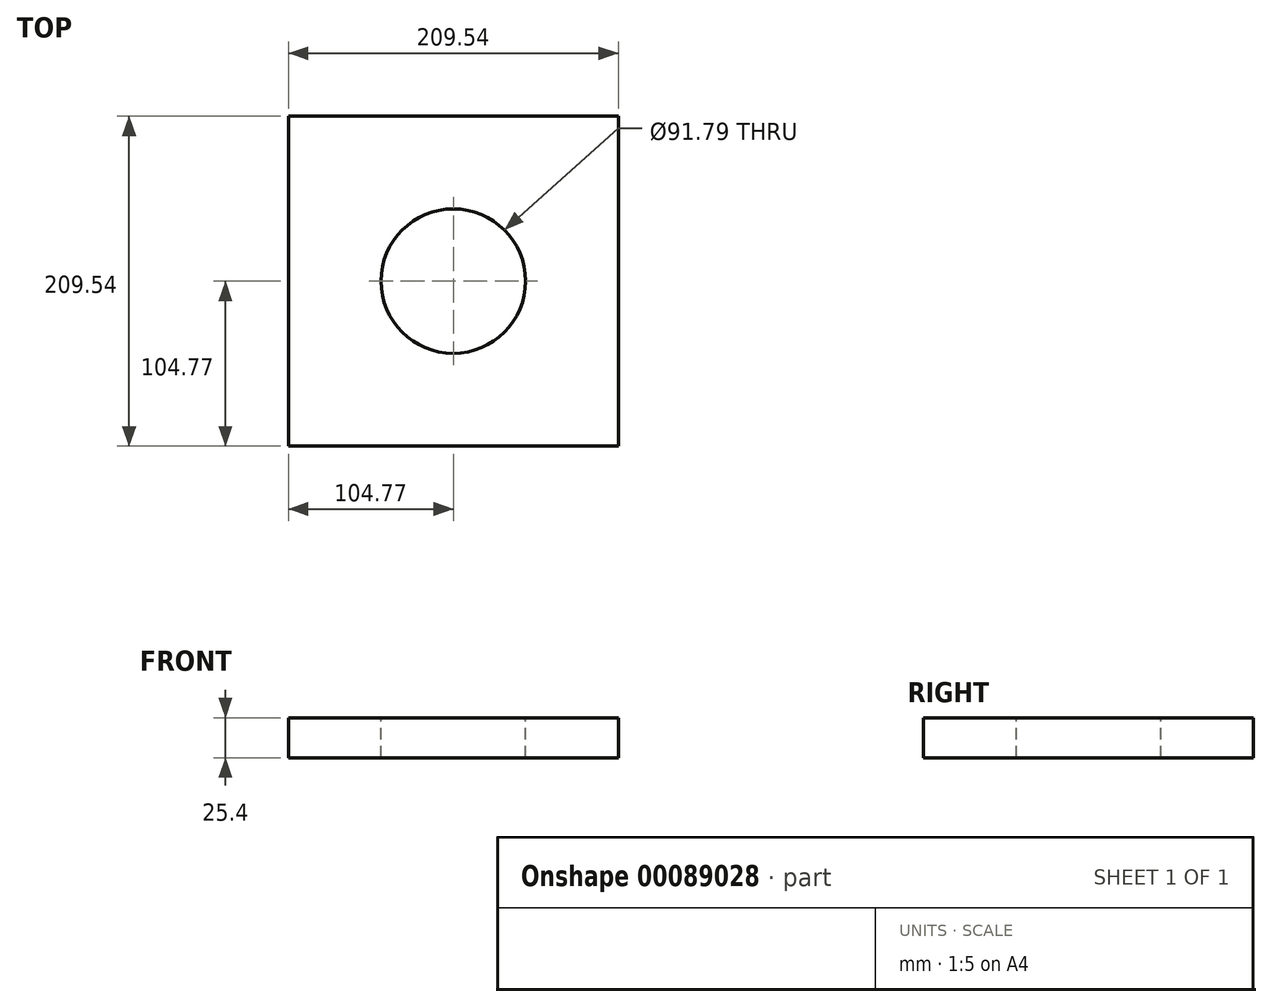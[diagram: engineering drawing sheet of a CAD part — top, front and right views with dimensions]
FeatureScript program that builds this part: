
annotation { "Feature Type Name" : "Feature", "Feature Type Description" : "" }
export const myFeature = defineFeature(function(context is Context, id is Id, definition is map)
    precondition{}
    {
        {
            var Q0;
            Q0=qCreatedBy(makeId("Top.planeOp"),FACE);
            var sketch = newSketch(context, id + "F0", { "sketchPlane" : qUnion([Q0])});
            skLineSegment(sketch, "E0.bottom", {"start": v(-104.78, -104.77) * mm, "end": v(104.78, -104.77) * mm});
            skLineSegment(sketch, "E0.top", {"start": v(-104.78, 104.78) * mm, "end": v(104.77, 104.78) * mm});
            skLineSegment(sketch, "E0.left", {"start": v(-104.77, -104.77) * mm, "end": v(-104.78, 104.78) * mm});
            skLineSegment(sketch, "E0.right", {"start": v(104.78, -104.77) * mm, "end": v(104.78, 104.78) * mm});
            skPoint(sketch, "E0.middle", {"position": v(0, 0) * mm});
            skCircle(sketch, "E1", {"center": v(0, 0) * mm, "radius": 32.18 * mm});
            skCircle(sketch, "E2.0", {"center": v(0, 0) * mm, "radius": 45.9 * mm});
            skSolve(sketch);
        }
        {
            var Q0;
            Q0=makeQuery(id+"F0.imprint","IMPRINT",FACE,{"disambiguationData":[TD([[makeQuery(id+"F0.imprint","IMPRINT",EDGE,{"derivedFrom":sQuery(id+"F0.wireOp",EDGE,"E0.bottom")}),1.0]])]});
            extrude(context, id + "F1", {"entities" : qUnion([Q0]), "oppositeDirection" : true, "depth" : 25.4 * mm});
        }
    });
